# Revit family: FMS1_63_UN_Surface-mounted_ETK
name_source: partatom
category: Lighting Fixtures
units: mm (PartAtom-declared; Revit-internal decimal feet)

## family parameters
Always vertical = Yes
Cut with Voids When Loaded = No
Light Source = No
OmniClass Number = 23.80.70.11.14.11
OmniClass Title = Downlights
Part Type = Normal
Room Calculation Point = Yes
Round Connector Dimension = Use Diameter
Shared = No
Work Plane-Based = No

## types (14) — shared parameters
Assembly Code = 63.0
Bundle = 110°
Description = Surface Mounted
IfcExportAs = IfcLightFixtureType
IfcExportType = USERDEFINED
Lamp = LED
Luminaire_Body_Material = PPS Plastic
Manufacturer = ETK licht B.V.
Model = FMK.1
Type Comments = IP20
URL = https://www.etk.nl
Voltage = 230 V

## per-type parameters (varying)
| type | 43mm Height | 63mm Height | Apparent Load | Diameter | Light Source | Radius | Wattage Comments |
| FMS.1100.10 - Ø270 / 18W / 1120lm / 3000K | Yes | No | 18 VA | 270 mm  [stored 0.885827 ft] | FMS.1 - Lightsource : FMS.1100.10 - Ø270 / 18W / 1120lm / 3000K | 135 mm  [stored 0.442913 ft] | 18W |
| FMS.1110.10 - Ø270 / 18W / 1120lm / 4000K | Yes | No | 18 VA | 270 mm  [stored 0.885827 ft] | FMS.1 - Lightsource : FMS.1110.10 - Ø270 / 18W / 1120lm / 4000K | 135 mm  [stored 0.442913 ft] | 18W |
| FMS.1140.10 - Ø270 / 18W / 1120lm / 3000K | Yes | No | 18 VA | 270 mm  [stored 0.885827 ft] | FMS.1 - Lightsource : FMS.1140.10 - Ø270 / 18W / 1120lm / 3000K | 135 mm  [stored 0.442913 ft] | 18W |
| FMS.1150.10 - Ø270 / 18W / 1120lm / 4000K | Yes | No | 18 VA | 270 mm  [stored 0.885827 ft] | FMS.1 - Lightsource : FMS.1150.10 - Ø270 / 18W / 1120lm / 4000K | 135 mm  [stored 0.442913 ft] | 18W |
| FMS.1100.10N - Ø270 / 18W / 1120lm / 3000K | Yes | No | 18 VA | 270 mm  [stored 0.885827 ft] | FMS.1 - Lightsource : FMS.1100.10N - Ø270 / 18W / 1120lm / 3000K | 135 mm  [stored 0.442913 ft] | 18W |
| FMS.1110.10N - Ø270 / 18W / 1120lm / 4000K | Yes | No | 18 VA | 270 mm  [stored 0.885827 ft] | FMS.1 - Lightsource : FMS.1110.10N - Ø270 / 18W / 1120lm / 4000K | 135 mm  [stored 0.442913 ft] | 18W |
| FMS.1103.10 - Ø270 / 18W / 1120lm / 3000K | Yes | No | 18 VA | 270 mm  [stored 0.885827 ft] | FMS.1 - Lightsource : FMS.1103.10 - Ø270 / 18W / 1120lm / 3000K | 135 mm  [stored 0.442913 ft] | 18W |
| FMS.1113.10 - Ø270 / 18W / 1120lm / 4000K | Yes | No | 18 VA | 270 mm  [stored 0.885827 ft] | FMS.1 - Lightsource : FMS.1113.10 - Ø270 / 18W / 1120lm / 4000K | 135 mm  [stored 0.442913 ft] | 18W |
| FMS.1400.10 - Ø400 / 38W / 2800lm / 3000K | No | Yes | 38 VA | 400 mm  [stored 1.31234 ft] | FMS.1 - Lightsource : FMS.1400.10 - Ø400 / 38W / 2800lm / 3000K | 200 mm  [stored 0.656168 ft] | 38W |
| FMS.1410.10 - Ø400 / 38W / 2800lm / 4000K | No | Yes | 38 VA | 400 mm  [stored 1.31234 ft] | FMS.1 - Lightsource : FMS.1410.10 - Ø400 / 38W / 2800lm / 4000K | 200 mm  [stored 0.656168 ft] | 38W |
| FMS.1400.10N - Ø400 / 38W / 2800lm / 3000K | No | Yes | 38 VA | 400 mm  [stored 1.31234 ft] | FMS.1 - Lightsource : FMS.1400.10N - Ø400 / 38W / 2800lm / 3000K | 200 mm  [stored 0.656168 ft] | 38W |
| FMS.1410N.10 - Ø400 / 38W / 2800lm / 4000K | No | Yes | 38 VA | 400 mm  [stored 1.31234 ft] | FMS.1 - Lightsource : FMS.1410.10N - Ø400 / 38W / 2800lm / 4000K | 200 mm  [stored 0.656168 ft] | 38W |
| FMS.1403.10 - Ø400 / 38W / 2800lm / 3000K | No | Yes | 38 VA | 400 mm  [stored 1.31234 ft] | FMS.1 - Lightsource : FMS.1403.10 - Ø400 / 38W / 2800lm / 3000K | 200 mm  [stored 0.656168 ft] | 38W |
| FMS.1413.10 - Ø400 / 38W / 2800lm / 4000K | No | Yes | 38 VA | 400 mm  [stored 1.31234 ft] | FMS.1 - Lightsource : FMS.1413.10 - Ø400 / 38W / 2800lm / 4000K | 200 mm  [stored 0.656168 ft] | 38W |

note: [stored X ft] marks values corroborated as IEEE doubles in the binary element streams (Revit-internal decimal feet)

## geometry (parser evidence)
native form markers: Sweep x9
no freeform markers — native parametric forms only
